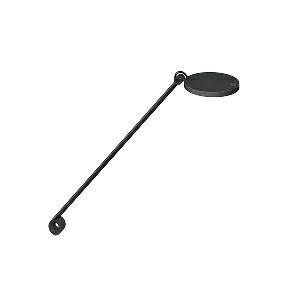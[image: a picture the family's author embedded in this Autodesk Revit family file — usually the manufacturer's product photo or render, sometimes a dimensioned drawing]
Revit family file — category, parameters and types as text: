
# Revit family: para_mi_-_mftl_102_r__930_00643776_62cd
name_source: partatom
category: Lighting Fixtures
units: mm (PartAtom-declared; Revit-internal decimal feet)

## family parameters
Cut with Voids When Loaded = No
Host = Face
Light Source = No
Part Type = Normal
Room Calculation Point = No
Round Connector Dimension = Use Diameter
Shared = No

## types (1)
- PARA.MI - MFTL 102 R /930 (1 x LED, 580 lm, 3000K)
    Apparent Load = 7 VA
    Approval mark = CE
    CIE Flux Codes = 69 94 99 100 100
    Color Rendering = 90-100
    Color Temperature = 3000K
    Control Gear = Electronic ballast
    Default Elevation = 1800 mm
    Description = MFTL 102 R|Task luminaire|light source: LED|work equipment: Electronic plug-in transformer|connected load: 100-240 V, 50/60 Hz|Power consumption: approx. 7 W|luminous flux: 580 lm|luminous efficacy: 82 lm/W|Illuminance efficiency factor: 107 lx/W|colour temperature: Warm white, ca. 3000 K|color rendering index (CRI): >= 90|chromaticity tolerance:  3 SDCM|class of protection: II with plug-in power supply, III without plug-in power supply|technology: Continuously dimmable|luminaire body|material: Aluminium|surface: Painted|colour: Black|lamp cover: Plastic, Clear|tubular sections|material: Tubular aluminium section|surface: Painted|colour: Jet black|weight (net): approx. 1.0 kg|mains lead: 3.00 m Mains plug BS 1363, CEE 7/XVI, NEMA 1-15P|Fastening: Adaptor (accessory), Table base (accessory), Table clamp (accessory), Tap16|glare control: Reflector|special features: Automatic switchoff adjustable, Push button in luminaire head, Behaviour at net recovery adjustable|Approval mark: C - ETL - US (F. CAN U. USA), VDE - ENEC SEP LIGHT & POWER SUPPLY UNIT|
    Height = 12 mm  [stored 0.0393701 ft]
    Lamp = 1 x LED
    Lamp Light Flux = 580 lm
    Lamp count = 1
    Length = 123 mm
    Luminous efficacy = 83 lm/W
    Manufacturer = Waldmann
    ModVariant = No
    Model = 00643776
    Mounting Place = Table
    Mounting Type = Surface mounted
    Number of Poles = 1
    OnlyDefault = Yes
    Power Factor = 1
    Product Name = PARA.MI - MFTL 102 R /930
    Product group = Task luminaire (office)
    ProductGroupID = 21
    Protection Class = Protection class II
    Protection Degree = IP 40
    RLX_Detail_Level = 1
    RLX_Emergency_Light_Flux = 0 lm
    RLX_Emergency_Type = 0
    RLX_Emergency_Type_DB = No
    RlxData = <blob elided: 58725 chars, md5=203f0616>
    Socket = socket
    Standby Power = 0 W
    System Light Flux = 580 lm
    System Power = 7 W
    Type Comments = Product without accessories
    Type Image = 113150000-00643978.jpg
    URL = http://relux.com
    VarID = ---
    Voltage = 230 V
    Voltage Range = 220-240 V
    Weight = 0.00 kg
    Width = 0 mm  [stored 0 ft]

note: [stored X ft] marks values corroborated as IEEE doubles in the binary element streams (Revit-internal decimal feet)

## geometry (parser evidence)
native form markers: Blend x4, Sweep x13
no freeform markers — native parametric forms only
